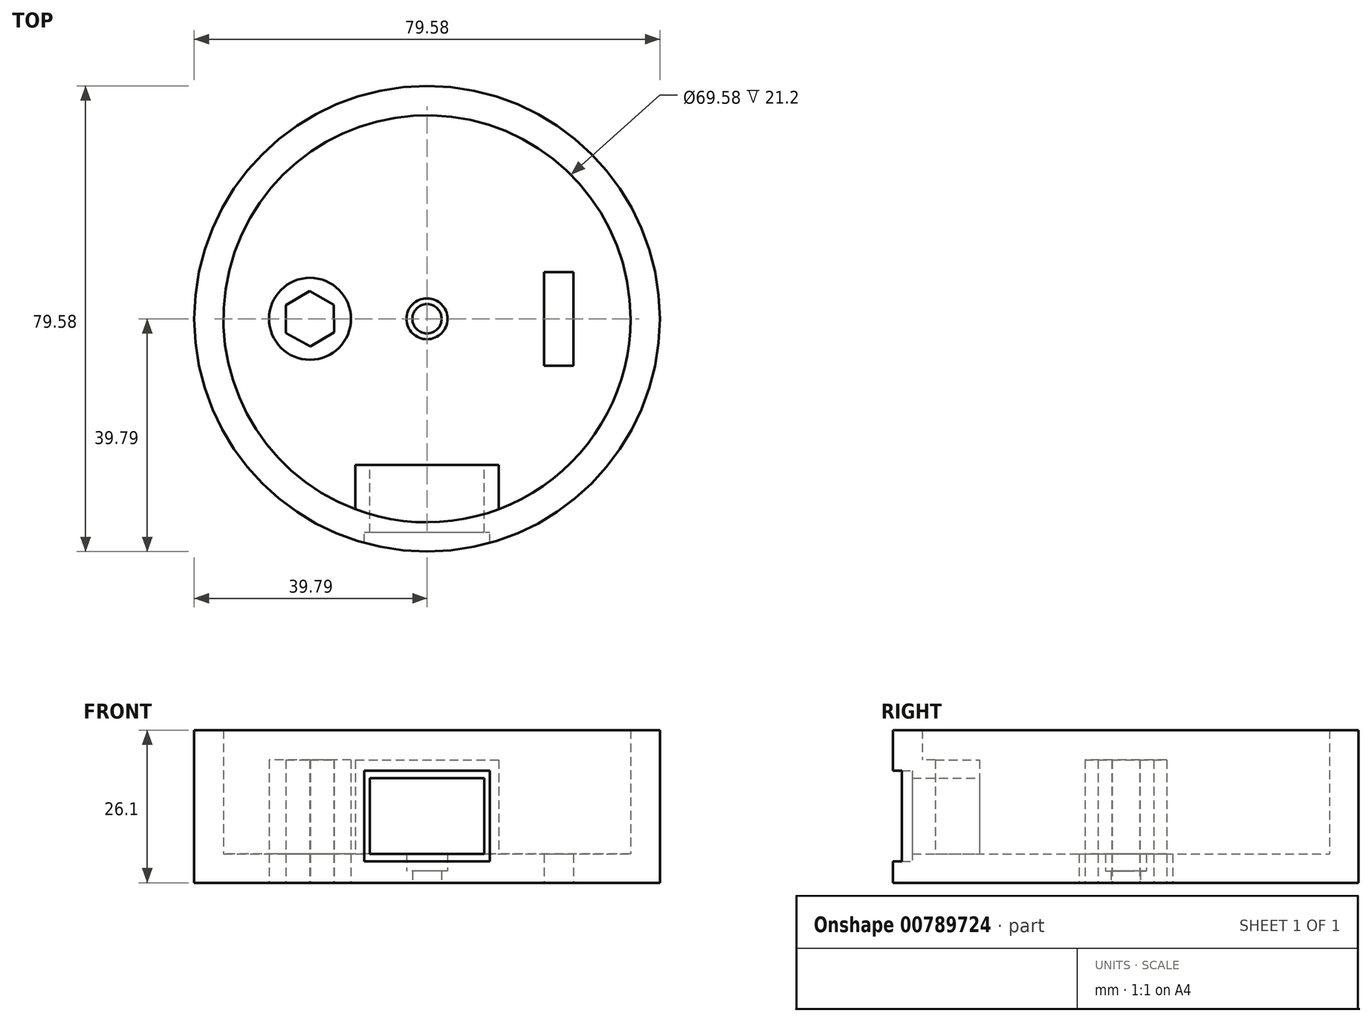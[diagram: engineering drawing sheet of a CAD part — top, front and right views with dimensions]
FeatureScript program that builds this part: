
annotation { "Feature Type Name" : "Feature", "Feature Type Description" : "" }
export const myFeature = defineFeature(function(context is Context, id is Id, definition is map)
    precondition{}
    {
        {
            var Q0;
            Q0=qCreatedBy(makeId("Top.planeOp"),FACE);
            var sketch = newSketch(context, id + "F0", { "sketchPlane" : qUnion([Q0])});
            skCircle(sketch, "E0", {"center": v(0, 0) * mm, "radius": 39.79 * mm});
            skCircle(sketch, "E1", {"center": v(0, 0) * mm, "radius": 3.5 * mm});
            skCircle(sketch, "E2", {"center": v(0, 0) * mm, "radius": 34.79 * mm});
            skCircle(sketch, "E3", {"center": v(0, 0) * mm, "radius": 2.5 * mm});
            skLineSegment(sketch, "E4.bottom", {"start": v(20, 8) * mm, "end": v(25, 8) * mm});
            skLineSegment(sketch, "E4.left", {"start": v(20, 8) * mm, "end": v(20, 4.1) * mm});
            skLineSegment(sketch, "E4.right", {"start": v(25, 8) * mm, "end": v(25, 5) * mm});
            skLineSegment(sketch, "E5.MirrorCS", {"start": v(25, -8) * mm, "end": v(25, -5) * mm});
            skLineSegment(sketch, "E6.MirrorCS", {"start": v(20, -8) * mm, "end": v(25, -8) * mm});
            skLineSegment(sketch, "E7.MirrorCS", {"start": v(20, -8) * mm, "end": v(20, -4.1) * mm});
            skCircle(sketch, "E8.cCircle", {"center": v(-20, 0) * mm, "radius": 4.75 * mm, "construction": true});
            skLineSegment(sketch, "E8.0", {"start": v(-24.1, -2.41) * mm, "end": v(-24.13, 2.34) * mm});
            skLineSegment(sketch, "E8.1", {"start": v(-24.13, 2.34) * mm, "end": v(-20.04, 4.75) * mm});
            skLineSegment(sketch, "E8.2", {"start": v(-20.04, 4.75) * mm, "end": v(-15.9, 2.41) * mm});
            skLineSegment(sketch, "E8.3", {"start": v(-15.9, 2.41) * mm, "end": v(-15.87, -2.34) * mm});
            skLineSegment(sketch, "E8.4", {"start": v(-15.87, -2.34) * mm, "end": v(-19.96, -4.75) * mm});
            skLineSegment(sketch, "E8.5", {"start": v(-19.96, -4.75) * mm, "end": v(-24.1, -2.41) * mm});
            skCircle(sketch, "E9", {"center": v(-20, 0) * mm, "radius": 7 * mm});
            skLineSegment(sketch, "E10.left", {"start": v(20, 8) * mm, "end": v(20, -8) * mm});
            skLineSegment(sketch, "E10.right", {"start": v(25, 8) * mm, "end": v(25, -8) * mm});
            skSolve(sketch);
        }
        {
            var Q0;
            Q0=makeQuery(id+"F0.imprint","IMPRINT",FACE,{"disambiguationData":[TD([[makeQuery(id+"F0.imprint","IMPRINT",EDGE,{"derivedFrom":sQuery(id+"F0.wireOp",EDGE,"E0")}),1.0]])]});
            var Q1;
            Q1 = qSketchRegion(id + "F5", true);
            extrude(context, id + "F1", {"entities" : qUnion([Q0, Q1]), "depth" : 26.1 * mm, "offsetDistance" : 25 * mm});
        }
        {
            var Q0;
            Q0=makeQuery(id+"F0.imprint","IMPRINT",FACE,{"disambiguationData":[TD([[makeQuery(id+"F0.imprint","IMPRINT",EDGE,{"derivedFrom":sQuery(id+"F0.wireOp",EDGE,"E1")}),-1.0]])]});
            var Q1;
            Q1=makeQuery(id+"F0.imprint","IMPRINT",FACE,{"disambiguationData":[TD([[makeQuery(id+"F0.imprint","IMPRINT",EDGE,{"derivedFrom":sQuery(id+"F0.wireOp",EDGE,"E8.0")}),-1.0]])]});
            extrude(context, id + "F2", {"entities" : qUnion([Q0, Q1]), "operationType" : NewBodyOperationType.ADD, "depth" : 4.9 * mm, "offsetDistance" : 25 * mm});
        }
        {
            var Q0;
            Q0=makeQuery(id+"F0.imprint","IMPRINT",FACE,{"disambiguationData":[TD([[makeQuery(id+"F0.imprint","IMPRINT",EDGE,{"derivedFrom":sQuery(id+"F0.wireOp",EDGE,"E1")}),1.0]])]});
            extrude(context, id + "F3", {"entities" : qUnion([Q0]), "operationType" : NewBodyOperationType.ADD, "depth" : 2 * mm, "offsetDistance" : 25 * mm});
        }
        {
            var Q0;
            Q0=makeQuery(id+"F0.imprint","IMPRINT",FACE,{"disambiguationData":[TD([[makeQuery(id+"F0.imprint","IMPRINT",EDGE,{"derivedFrom":sQuery(id+"F0.wireOp",EDGE,"E8.0")}),1.0]])]});
            extrude(context, id + "F4", {"entities" : qUnion([Q0]), "depth" : 21 * mm, "offsetDistance" : 25 * mm});
        }
        {
            var Q0;
            Q0=qCreatedBy(makeId("Front.planeOp"),FACE);
            var sketch = newSketch(context, id + "F5", { "sketchPlane" : qUnion([Q0])});
            skLineSegment(sketch, "E11.bottom", {"start": v(-9.8, 17.9) * mm, "end": v(9.8, 17.9) * mm});
            skLineSegment(sketch, "E11.top", {"start": v(-9.8, 4.9) * mm, "end": v(9.8, 4.9) * mm});
            skLineSegment(sketch, "E11.left", {"start": v(-9.8, 17.9) * mm, "end": v(-9.8, 4.9) * mm});
            skLineSegment(sketch, "E11.right", {"start": v(9.8, 17.9) * mm, "end": v(9.8, 4.9) * mm});
            skLineSegment(sketch, "E12.bottom", {"start": v(-10.75, 19.15) * mm, "end": v(10.75, 19.15) * mm});
            skLineSegment(sketch, "E12.top", {"start": v(-10.75, 3.65) * mm, "end": v(10.75, 3.65) * mm});
            skLineSegment(sketch, "E12.left", {"start": v(-10.75, 19.15) * mm, "end": v(-10.75, 3.65) * mm});
            skLineSegment(sketch, "E12.right", {"start": v(10.75, 19.15) * mm, "end": v(10.75, 3.65) * mm});
            skLineSegment(sketch, "E13", {"start": v(-11.66, 11.4) * mm, "end": v(17.48, 11.4) * mm, "construction": true});
            skLineSegment(sketch, "E14.bottom", {"start": v(-12.25, 21) * mm, "end": v(12.25, 21) * mm});
            skLineSegment(sketch, "E14.top", {"start": v(-12.25, 3.65) * mm, "end": v(12.25, 3.65) * mm});
            skLineSegment(sketch, "E14.left", {"start": v(-12.25, 21) * mm, "end": v(-12.25, 3.65) * mm});
            skLineSegment(sketch, "E14.right", {"start": v(12.25, 21) * mm, "end": v(12.25, 3.65) * mm});
            skSolve(sketch);
        }
        {
            var Q0;
            Q0=makeQuery(id+"F5.imprint","IMPRINT",FACE,{"disambiguationData":[TD([[makeQuery(id+"F5.imprint","IMPRINT",EDGE,{"derivedFrom":sQuery(id+"F5.wireOp",EDGE,"E11.bottom")}),-1.0]])]});
            extrude(context, id + "F6", {"entities" : qUnion([Q0]), "operationType" : NewBodyOperationType.REMOVE, "depth" : 45 * mm, "offsetDistance" : 25 * mm, "hasSecondDirection" : true, "secondDirectionOppositeDirection" : true, "secondDirectionDepth" : -25 * mm});
        }
        {
            var Q0;
            Q0=makeQuery(id+"F5.imprint","IMPRINT",FACE,{"disambiguationData":[TD([[makeQuery(id+"F5.imprint","IMPRINT",EDGE,{"derivedFrom":sQuery(id+"F5.wireOp",EDGE,"E11.bottom")}),1.0]])]});
            extrude(context, id + "F7", {"entities" : qUnion([Q0]), "operationType" : NewBodyOperationType.REMOVE, "depth" : 45 * mm, "offsetDistance" : 25 * mm, "hasSecondDirection" : true, "secondDirectionOppositeDirection" : true, "secondDirectionDepth" : -36.5 * mm});
        }
        {
            var Q0;
            Q0=makeQuery(id+"F5.imprint","IMPRINT",FACE,{"disambiguationData":[TD([[makeQuery(id+"F5.imprint","IMPRINT",EDGE,{"derivedFrom":sQuery(id+"F5.wireOp",EDGE,"E11.bottom")}),1.0]])]});
            extrude(context, id + "F8", {"entities" : qUnion([Q0]), "depth" : 36.5 * mm, "offsetDistance" : 25 * mm, "hasSecondDirection" : true, "secondDirectionOppositeDirection" : true, "secondDirectionDepth" : -25 * mm});
        }
        {
            var Q0;
            Q0=makeQuery(id+"F5.imprint","IMPRINT",FACE,{"disambiguationData":[TD([[makeQuery(id+"F5.imprint","IMPRINT",EDGE,{"derivedFrom":sQuery(id+"F5.wireOp",EDGE,"E12.bottom")}),1.0]])]});
            extrude(context, id + "F9", {"entities" : qUnion([Q0]), "operationType" : NewBodyOperationType.ADD, "depth" : 36.5 * mm, "offsetDistance" : 25 * mm, "hasSecondDirection" : true, "secondDirectionOppositeDirection" : true, "secondDirectionDepth" : -25 * mm});
        }
    });
